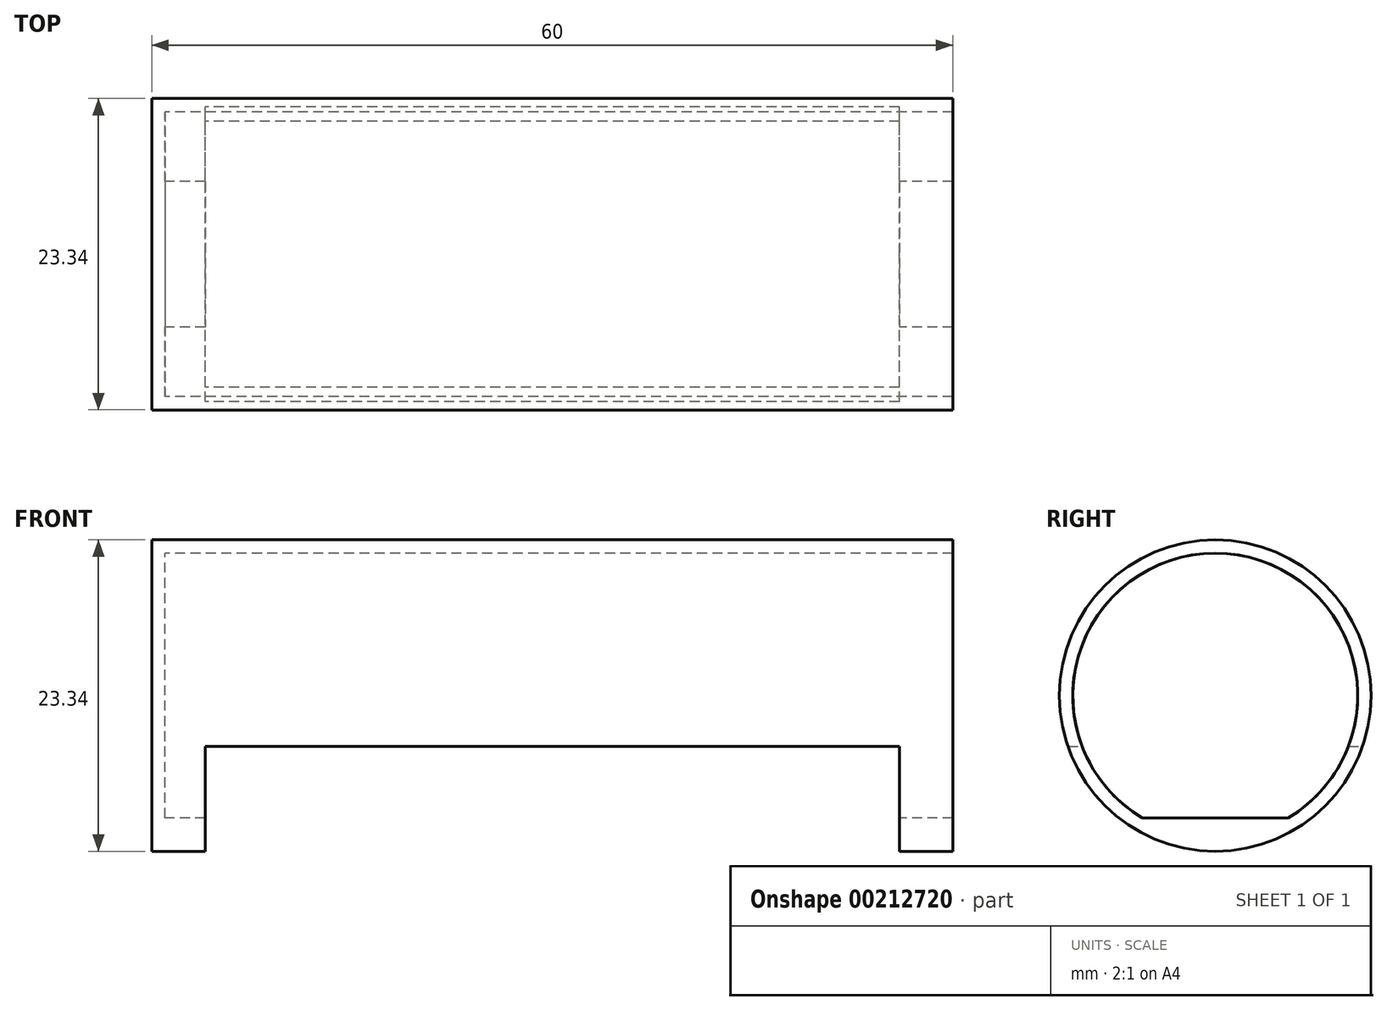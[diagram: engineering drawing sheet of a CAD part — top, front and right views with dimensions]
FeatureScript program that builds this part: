
annotation { "Feature Type Name" : "Feature", "Feature Type Description" : "" }
export const myFeature = defineFeature(function(context is Context, id is Id, definition is map)
    precondition{}
    {
        {
            var Q0;
            Q0=qCreatedBy(makeId("Right.planeOp"),FACE);
            var sketch = newSketch(context, id + "F0", { "sketchPlane" : qUnion([Q0])});
            skCircle(sketch, "E0", {"center": v(0, 0) * mm, "radius": 10.67 * mm});
            skLineSegment(sketch, "E1", {"start": v(-9.25, 5.33) * mm, "end": v(9.25, 5.33) * mm, "construction": true});
            skCircle(sketch, "E2.0", {"center": v(0, 0) * mm, "radius": 11.67 * mm});
            skLineSegment(sketch, "E3", {"start": v(0, 5.33) * mm, "end": v(0, -10.67) * mm, "construction": true});
            skLineSegment(sketch, "E4", {"start": v(5.46, -9.17) * mm, "end": v(-5.46, -9.17) * mm});
            skLineSegment(sketch, "E5", {"start": v(-2.64, 5.33) * mm, "end": v(-2.64, -9.17) * mm, "construction": true});
            skSolve(sketch);
        }
        {
            var Q0;
            Q0=makeQuery(id+"F0.imprint","IMPRINT",FACE,{"disambiguationData":[TD([[makeQuery(id+"F0.imprint","IMPRINT",EDGE,{"derivedFrom":sQuery(id+"F0.wireOp",EDGE,"E0")}),-1.0]])]});
            var Q1;
            {var subQ0=sQuery(id+"F0.wireOp",EDGE,"E4");Q1=makeQuery(id+"F0.imprint","IMPRINT",FACE,{"disambiguationData":[TD([[makeQuery(id+"F0.imprint","IMPRINT",EDGE,{"derivedFrom":subQ0}),1.0]])]});}
            extrude(context, id + "F1", {"entities" : qUnion([Q0, Q1]), "depth" : 60 * mm, "offsetDistance" : 25 * mm});
        }
        {
            var Q0;
            Q0=qCreatedBy(makeId("Top.planeOp"),FACE);
            var sketch = newSketch(context, id + "F2", { "sketchPlane" : qUnion([Q0])});
            skLineSegment(sketch, "E6.bottom", {"start": v(4, -14.16) * mm, "end": v(56, -14.16) * mm});
            skLineSegment(sketch, "E6.top", {"start": v(4, 14.16) * mm, "end": v(56, 14.16) * mm});
            skLineSegment(sketch, "E6.left", {"start": v(4, -14.16) * mm, "end": v(4, 14.16) * mm});
            skLineSegment(sketch, "E6.right", {"start": v(56, -14.16) * mm, "end": v(56, 14.16) * mm});
            skLineSegment(sketch, "E7.0", {"start": v(60, 11.67) * mm, "end": v(60, -11.67) * mm, "construction": true});
            skLineSegment(sketch, "E8", {"start": v(56, 0) * mm, "end": v(60, 0) * mm, "construction": true});
            skLineSegment(sketch, "E9", {"start": v(0, 0) * mm, "end": v(4, 0) * mm, "construction": true});
            skSolve(sketch);
        }
        {
            var Q0;
            Q0 = qSketchRegion(id + "F2", true);
            extrude(context, id + "F3", {"entities" : qUnion([Q0]), "operationType" : NewBodyOperationType.REMOVE, "oppositeDirection" : true, "depth" : 13.1 * mm, "offsetDistance" : 25 * mm, "hasSecondDirection" : true, "secondDirectionOppositeDirection" : true, "secondDirectionDepth" : 3.8 * mm});
        }
        {
            var Q0;
            {var subQ0=sQuery(id+"F0.wireOp",EDGE,"E4");Q0=makeQuery(id+"F0.imprint","IMPRINT",FACE,{"disambiguationData":[TD([[makeQuery(id+"F0.imprint","IMPRINT",EDGE,{"derivedFrom":subQ0}),-1.0]])]});}
            var sketch = newSketch(context, id + "F4", { "sketchPlane" : qUnion([Q0])});
            skCircle(sketch, "E10.0", {"center": v(0, 0) * mm, "radius": 11.67 * mm});
            skSolve(sketch);
        }
        {
            var Q0;
            Q0 = qSketchRegion(id + "F4", true);
            extrude(context, id + "F5", {"entities" : qUnion([Q0]), "operationType" : NewBodyOperationType.ADD, "depth" : 1 * mm, "offsetDistance" : 25 * mm});
        }
    });
